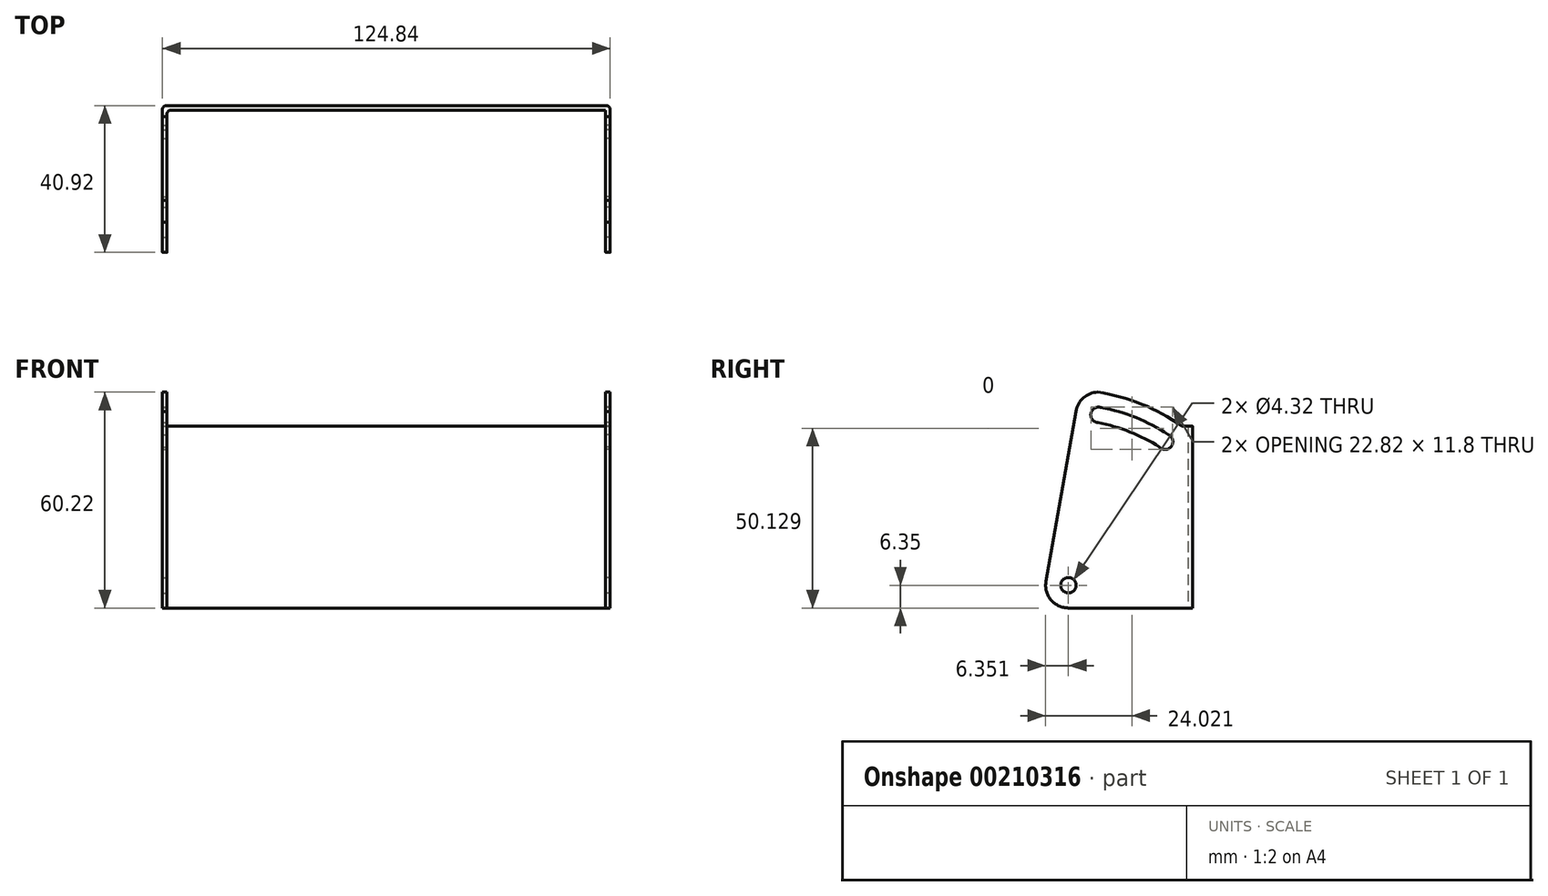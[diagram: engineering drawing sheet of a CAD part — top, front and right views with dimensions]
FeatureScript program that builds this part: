
annotation { "Feature Type Name" : "Feature", "Feature Type Description" : "" }
export const myFeature = defineFeature(function(context is Context, id is Id, definition is map)
    precondition{}
    {
        {
            var Q0;
            Q0=qCreatedBy(makeId("Front.planeOp"),FACE);
            var sketch = newSketch(context, id + "F0", { "sketchPlane" : qUnion([Q0])});
            skLineSegment(sketch, "E0.bottom", {"start": v(61.15, 25.4) * mm, "end": v(-61.15, 25.4) * mm});
            skLineSegment(sketch, "E0.top", {"start": v(61.15, -25.4) * mm, "end": v(-61.15, -25.4) * mm});
            skLineSegment(sketch, "E0.left", {"start": v(61.15, 25.4) * mm, "end": v(61.15, -25.4) * mm});
            skLineSegment(sketch, "E0.right", {"start": v(-61.15, 25.4) * mm, "end": v(-61.15, -25.4) * mm});
            skPoint(sketch, "E0.middle", {"position": v(0, 0) * mm});
            skSolve(sketch);
        }
        {
            var Q0;
            Q0 = qSketchRegion(id + "F0", true);
            extrude(context, id + "F1", {"entities" : qUnion([Q0]), "depth" : 1.27 * mm});
        }
        {
            var Q0;
            Q0=makeQuery(id+"F1.opExtrude","SWEPT_FACE",FACE,{"disambiguationData":[OSD([sQuery(id+"F0.wireOp",EDGE,"E0.left")])]});
            var sketch = newSketch(context, id + "F2", { "sketchPlane" : qUnion([Q0])});
            skLineSegment(sketch, "E1.bottom", {"start": v(0, -25.4) * mm, "end": v(-34.57, -25.4) * mm});
            skPoint(sketch, "E2.visualSharp", {"position": v(-42.14, -25.4) * mm});
            skArc(sketch, "E2.filletArc", {"start": v(-40.82, -17.95) * mm, "mid": v(-39.43, -23.13) * mm, "end": v(-34.57, -25.4) * mm});
            skCircle(sketch, "E3", {"center": v(-34.57, -19.05) * mm, "radius": 2.16 * mm});
            skLineSegment(sketch, "E4", {"start": v(0, 25.4) * mm, "end": v(-3.05, 25.4) * mm});
            skArc(sketch, "E5", {"start": v(-25.43, 30.5) * mm, "mid": v(-28.3, 28.97) * mm, "end": v(-26.4, 26.33) * mm});
            skArc(sketch, "E6", {"start": v(-9.18, 19.5) * mm, "mid": v(-5.86, 19.73) * mm, "end": v(-6.72, 22.95) * mm});
            skArc(sketch, "E7", {"start": v(-3.05, 25.4) * mm, "mid": v(-14.16, 31.48) * mm, "end": v(-26.38, 34.82) * mm});
            skArc(sketch, "E8", {"start": v(-23.84, 34.37) * mm, "mid": v(-29.35, 33.99) * mm, "end": v(-32.47, 29.43) * mm});
            skLineSegment(sketch, "E9", {"start": v(-40.82, -17.95) * mm, "end": v(-32.47, 29.43) * mm});
            skArc(sketch, "E10", {"start": v(-6.72, 22.95) * mm, "mid": v(-15.68, 27.71) * mm, "end": v(-25.43, 30.5) * mm});
            skArc(sketch, "E11", {"start": v(-8.36, 18.95) * mm, "mid": v(-17, 23.56) * mm, "end": v(-26.4, 26.33) * mm});
            skSolve(sketch);
        }
        {
            var Q0;
            {var subQ1=sQuery(id+"F0.wireOp",EDGE,"E0.left");var subQ2=makeQuery(id+"F1.opExtrude","CAP_EDGE",EDGE,{"disambiguationData":[OSD([subQ1])],"isStart":true});Q0=makeQuery(id+"F2.imprint","IMPRINT",FACE,{"disambiguationData":[TD([[makeQuery(id+"F2.imprint","IMPRINT",EDGE,{"derivedFrom":subQ2}),-1.0]])]});}
            var Q1;
            {var subQ12=sQuery(id+"F2.wireOp",EDGE,"E2.filletArc");Q1=makeQuery(id+"F2.imprint","IMPRINT",FACE,{"disambiguationData":[TD([[makeQuery(id+"F2.imprint","IMPRINT",EDGE,{"derivedFrom":subQ12}),1.0]])]});}
            extrude(context, id + "F3", {"entities" : qUnion([Q0, Q1]), "operationType" : NewBodyOperationType.ADD, "depth" : 1.27 * mm});
        }
        {
            var Q0;
            Q0=makeQuery(id+"F1.opExtrude","SWEPT_BODY",BODY,{"disambiguationData":[OSD([sQuery(id+"F0.wireOp",EDGE,"E0.bottom"),sQuery(id+"F0.wireOp",EDGE,"E0.top"),sQuery(id+"F0.wireOp",EDGE,"E0.left"),sQuery(id+"F0.wireOp",EDGE,"E0.right")])]});
            var Q1;
            Q1=qCreatedBy(makeId("Right.planeOp"),FACE);
            mirror(context, id + "F4", {"operationType" : NewBodyOperationType.ADD, "entities" : qUnion([Q0]), "mirrorPlane" : qUnion([Q1])});
        }
        {
            var Q0;
            Q0=makeQuery(id+"F4.opPattern","COPY",EDGE,{"derivedFrom":makeQuery(id+"F3.opExtrude","CAP_EDGE",EDGE,{"disambiguationData":[OSD([sQuery(id+"F0.wireOp",EDGE,"E0.left")])],"isStart":false}),"instanceName":"1"});
            var Q1;
            Q1=makeQuery(id+"F3.opExtrude","CAP_EDGE",EDGE,{"disambiguationData":[OSD([sQuery(id+"F0.wireOp",EDGE,"E0.left")])],"isStart":false});
            var Q2;
            Q2=makeQuery(id+"F1.opExtrude","CAP_EDGE",EDGE,{"disambiguationData":[OSD([sQuery(id+"F0.wireOp",EDGE,"E0.left")])],"isStart":false});
            var Q3;
            Q3=makeQuery(id+"F4.boolean.opBoolean","MERGE",EDGE,{"derivedFrom":[makeQuery(id+"F1.opExtrude","CAP_EDGE",EDGE,{"disambiguationData":[OSD([sQuery(id+"F0.wireOp",EDGE,"E0.right")])],"isStart":false}),makeQuery(id+"F4.opPattern","COPY",EDGE,{"derivedFrom":makeQuery(id+"F1.opExtrude","CAP_EDGE",EDGE,{"disambiguationData":[OSD([sQuery(id+"F0.wireOp",EDGE,"E0.left")])],"isStart":false}),"instanceName":"1"})]});
            fillet(context, id + "F5", {"entities" : qUnion([Q0, Q1, Q2, Q3]), "radius" : 1.02 * mm, "tangentPropagation" : true, "allowEdgeOverflow" : false});
        }
    });
